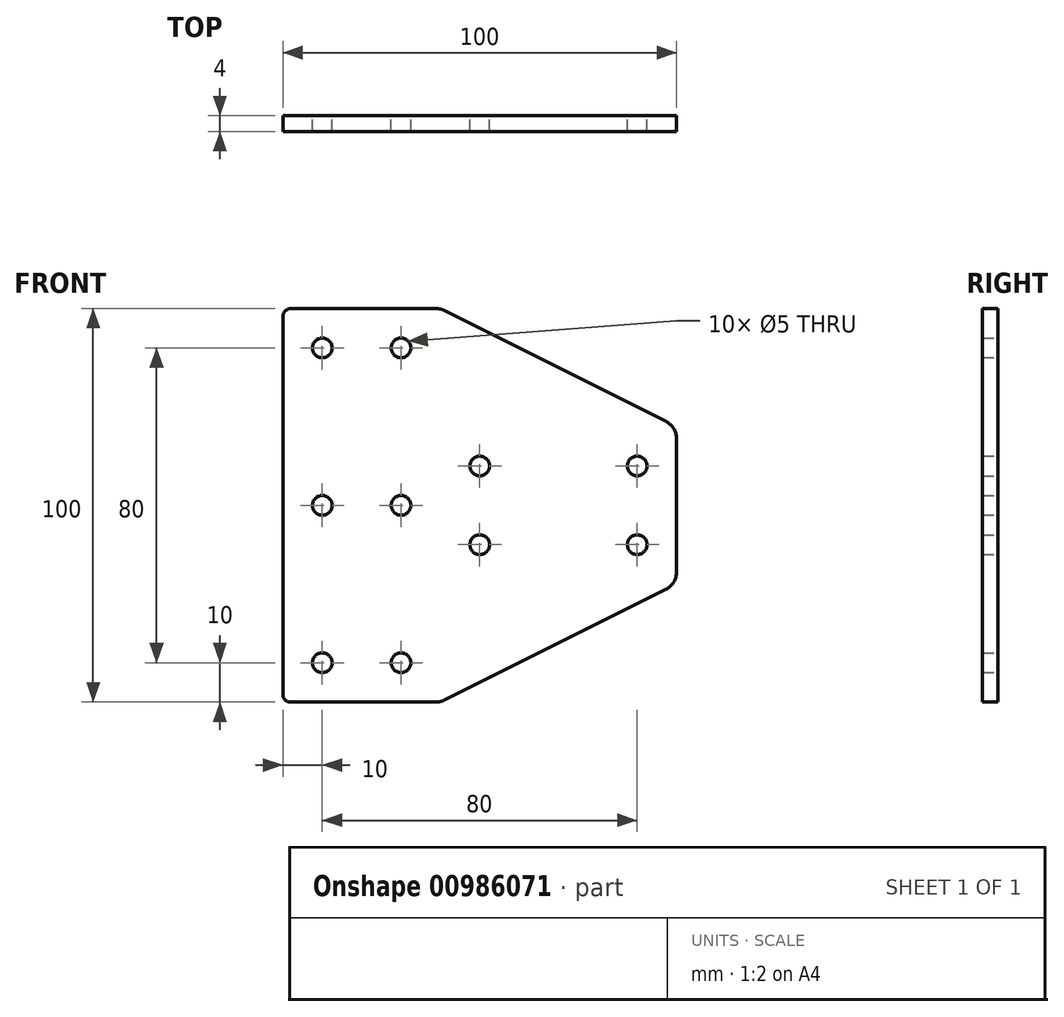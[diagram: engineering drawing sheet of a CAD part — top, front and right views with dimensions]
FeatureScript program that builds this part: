
annotation { "Feature Type Name" : "Feature", "Feature Type Description" : "" }
export const myFeature = defineFeature(function(context is Context, id is Id, definition is map)
    precondition{}
    {
        {
            var Q0;
            Q0=qCreatedBy(makeId("Front.planeOp"),FACE);
            var sketch = newSketch(context, id + "F0", { "sketchPlane" : qUnion([Q0])});
            skLineSegment(sketch, "E0", {"start": v(-10.04, 0) * mm, "end": v(100.77, 0) * mm, "construction": true});
            skLineSegment(sketch, "E1", {"start": v(0, 0) * mm, "end": v(0, 48) * mm});
            skLineSegment(sketch, "E2", {"start": v(2, 50) * mm, "end": v(38.82, 50) * mm});
            skLineSegment(sketch, "E3", {"start": v(41.06, 49.47) * mm, "end": v(97.24, 21.38) * mm});
            skLineSegment(sketch, "E4", {"start": v(100, 16.9) * mm, "end": v(100, 0) * mm});
            skLineSegment(sketch, "E5.MirrorCS", {"start": v(0, 0) * mm, "end": v(0, -48) * mm});
            skLineSegment(sketch, "E6.MirrorCS", {"start": v(2, -50) * mm, "end": v(38.82, -50) * mm});
            skLineSegment(sketch, "E7.MirrorCS", {"start": v(41.06, -49.47) * mm, "end": v(97.24, -21.38) * mm});
            skLineSegment(sketch, "E8.MirrorCS", {"start": v(100, -16.9) * mm, "end": v(100, 0) * mm});
            skLineSegment(sketch, "E9", {"start": v(10, 50) * mm, "end": v(10, -50) * mm, "construction": true});
            skPoint(sketch, "E9.endSnap0", {"position": v(20, -50) * mm});
            skLineSegment(sketch, "E10", {"start": v(30, 50) * mm, "end": v(30, -50) * mm, "construction": true});
            skLineSegment(sketch, "E11", {"start": v(40, 50) * mm, "end": v(40, -50) * mm, "construction": true});
            skLineSegment(sketch, "E12", {"start": v(100, 10) * mm, "end": v(40, 10) * mm, "construction": true});
            skLineSegment(sketch, "E13.MirrorCS", {"start": v(100, -10) * mm, "end": v(40, -10) * mm, "construction": true});
            skCircle(sketch, "E14", {"center": v(10, 0) * mm, "radius": 2.5 * mm});
            skCircle(sketch, "E15", {"center": v(30, 0) * mm, "radius": 2.5 * mm});
            skLineSegment(sketch, "E16", {"start": v(0, 40) * mm, "end": v(40, 40) * mm, "construction": true});
            skLineSegment(sketch, "E17.MirrorCS", {"start": v(0, -40) * mm, "end": v(40, -40) * mm, "construction": true});
            skCircle(sketch, "E18", {"center": v(10, 40) * mm, "radius": 2.5 * mm});
            skCircle(sketch, "E19", {"center": v(30, 40) * mm, "radius": 2.5 * mm});
            skCircle(sketch, "E20", {"center": v(10, -40) * mm, "radius": 2.5 * mm});
            skCircle(sketch, "E21", {"center": v(30, -40) * mm, "radius": 2.5 * mm});
            skLineSegment(sketch, "E22", {"start": v(50, 10) * mm, "end": v(50, -10) * mm, "construction": true});
            skLineSegment(sketch, "E23", {"start": v(90, 10) * mm, "end": v(90, -10) * mm, "construction": true});
            skCircle(sketch, "E24", {"center": v(50, 10) * mm, "radius": 2.5 * mm});
            skCircle(sketch, "E25", {"center": v(90, 10) * mm, "radius": 2.5 * mm});
            skCircle(sketch, "E26", {"center": v(90, -10) * mm, "radius": 2.5 * mm});
            skCircle(sketch, "E27", {"center": v(50, -10) * mm, "radius": 2.5 * mm});
            skPoint(sketch, "E28.visualSharp", {"position": v(40, 50) * mm});
            skArc(sketch, "E28.filletArc", {"start": v(41.06, 49.47) * mm, "mid": v(39.97, 49.87) * mm, "end": v(38.82, 50) * mm});
            skPoint(sketch, "E29.visualSharp", {"position": v(100, 20) * mm});
            skArc(sketch, "E29.filletArc", {"start": v(100, 16.9) * mm, "mid": v(99.25, 19.54) * mm, "end": v(97.24, 21.38) * mm});
            skPoint(sketch, "E30.visualSharp", {"position": v(100, -20) * mm});
            skArc(sketch, "E30.filletArc", {"start": v(97.24, -21.38) * mm, "mid": v(99.25, -19.54) * mm, "end": v(100, -16.9) * mm});
            skPoint(sketch, "E31.visualSharp", {"position": v(40, -50) * mm});
            skArc(sketch, "E31.filletArc", {"start": v(38.82, -50) * mm, "mid": v(39.97, -49.87) * mm, "end": v(41.06, -49.47) * mm});
            skPoint(sketch, "E32.visualSharp", {"position": v(0, 50) * mm});
            skArc(sketch, "E32.filletArc", {"start": v(2, 50) * mm, "mid": v(0.59, 49.41) * mm, "end": v(0, 48) * mm});
            skPoint(sketch, "E33.visualSharp", {"position": v(0, -50) * mm});
            skArc(sketch, "E33.filletArc", {"start": v(0, -48) * mm, "mid": v(0.59, -49.41) * mm, "end": v(2, -50) * mm});
            skSolve(sketch);
        }
        {
            var Q0;
            Q0=makeQuery(id+"F0.imprint","IMPRINT",FACE,{"disambiguationData":[TD([[makeQuery(id+"F0.imprint","IMPRINT",EDGE,{"derivedFrom":sQuery(id+"F0.wireOp",EDGE,"E1")}),-1.0]])]});
            extrude(context, id + "F1", {"entities" : qUnion([Q0]), "depth" : 4 * mm, "offsetDistance" : 25 * mm});
        }
    });
